# Revit family: OMNIDIABP1277
name_source: partatom
category: Communication Devices
revit_build: Autodesk Revit 2014 (Build: 20130308_1515(x64)
units: mm (PartAtom-declared; Revit-internal decimal feet)

## types (1)
- OMNIDIABP1277
    Assembly Code = D5090
    Base = Paint - Hubbell - Carbon Black
    Certifications = UL and cUL listed
    Coverage = 450 square foot
    Default Elevation = 48 "
    Description = The OMNIDIABP line voltage ceiling sensor combines passive infrared (PIR) and
acoustic (sound-activated) technologies to turn lighting systems on and off based
on occupancy. The OMNIDIABP features Hubbell Controls' patented IntelliDAPT®
technology, which makes all the sensor adjustments automatically.
    Features = IntelliDAPT self-adaptive technology—no manual adjustment required 
All-digital dual technology (acoustic and passive infrared [PIR]) sensor 
Non-volatile memory for sensor settings 
450 square-foot coverage 
Self-contained power supply
Universal voltage (120-277VAC; 50/60 Hz) 
UL and cUL listed 
California Title 24 compliant 
Five-year warranty 
120-277 Vac
    Housing Material = Paint - Hubbell - Matte White
    Manufacturer = Hubbell Control Solutions
    Model = OMNIDIABP1277
    Mounting = 8 - 12 Feet
    Output = 24 VDC active high-logic control signal with short circuit protection
    Power Requirment = 100-277VAC; 50/60Hz Single phase only
    Product Documentation Link = https://hubbellcdn.com
    Product Page URL = https://www.hubbell.com
    Sensing Element = Paint - Hubbell - Matte White
    Type Comments = CEILING MOUNT OCCUPANCY SENSORS
    URL = https://www.hubbell.com
    Warranty = 5-Years Warranty
    Width = 4.5 "

## geometry (parser evidence)
native form markers: Sweep x1
no freeform markers — native parametric forms only
